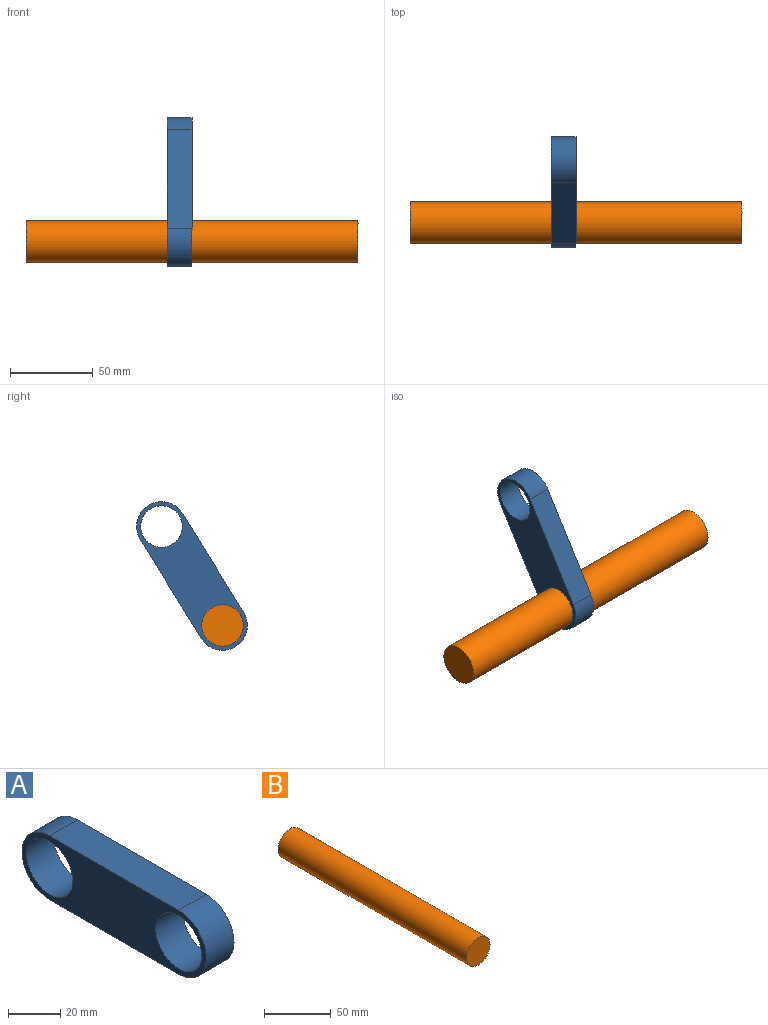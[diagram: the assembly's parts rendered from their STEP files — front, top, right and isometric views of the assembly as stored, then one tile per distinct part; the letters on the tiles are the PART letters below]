
ASSEMBLY  parts=2 mates=1
PART A: 8 faces, bbox 15x100x30 mm
  f0: plane 70x15mm, normal (0,0,1), area 1050mm2, adj f1,f3,f4,f5
  f1: cylinder r=15mm len=30mm, axis (-1,0,0), area 706.9mm2, adj f0,f2,f4,f5
  f2: plane 70x15mm, normal (0,0,-1), area 1050mm2, adj f1,f3,f4,f5
  f3: cylinder r=15mm len=30mm, axis (-1,0,0), area 706.9mm2, adj f0,f2,f4,f5
  f4: plane 100x30mm, normal (1,0,0), area 1825.1mm2, adj f0,f1,f2,f3,f6,f7
  f5: plane 100x30mm, normal (-1,0,0), area 1825.1mm2, adj f0,f1,f2,f3,f6,f7
  f6: cylinder r=12.5mm len=25mm, axis (-1,0,0), area 1178.1mm2, adj f4,f5
  f7: cylinder r=12.5mm len=25mm, axis (-1,0,0), area 1178.1mm2, adj f4,f5
PART B: 3 faces, bbox 25x200x25 mm
  f0: cylinder r=12.5mm len=200mm, axis (0,1,0), area 15708mm2, adj f1,f2
  f1: plane 25x25mm, normal (0,-1,0), area 490.9mm2, adj f0
  f2: plane 25x25mm, normal (0,1,0), area 490.9mm2, adj f0
PLACE A rot(axis=(1,0,0),58.3deg) t=(11.11,-1.9,-74.35)mm
PLACE B rot(axis=(0.44,0.44,-0.78),103.7deg) t=(126.11,-12.54,-67.79)mm
MATE cylindrical A.f1 <-> B.f0  axis (1,0,0) through (26.11,-12.54,-67.79)mm
